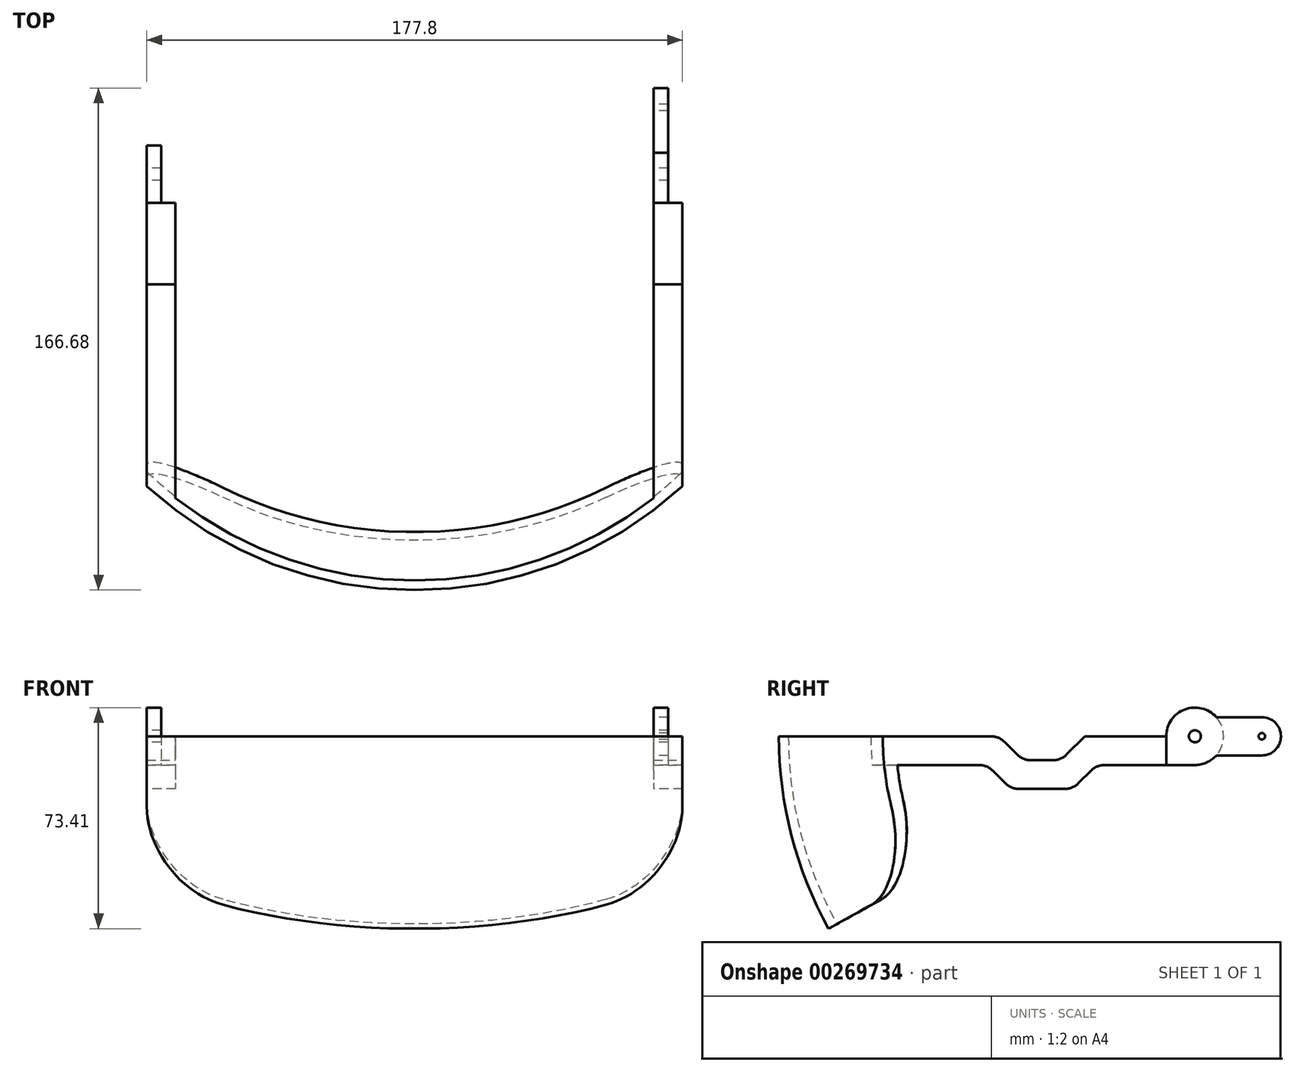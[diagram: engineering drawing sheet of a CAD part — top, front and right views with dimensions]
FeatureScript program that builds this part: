
annotation { "Feature Type Name" : "Feature", "Feature Type Description" : "" }
export const myFeature = defineFeature(function(context is Context, id is Id, definition is map)
    precondition{}
    {
        {
            var Q0;
            Q0=qCreatedBy(makeId("Right.planeOp"),FACE);
            var sketch = newSketch(context, id + "F0", { "sketchPlane" : qUnion([Q0])});
            skArc(sketch, "E0", {"start": v(0, 131.76) * mm, "mid": v(-131.76, 0) * mm, "end": v(0, -131.76) * mm});
            skArc(sketch, "E1", {"start": v(0, 128.59) * mm, "mid": v(-128.59, 0) * mm, "end": v(0, -128.59) * mm});
            skLineSegment(sketch, "E2", {"start": v(0, 131.76) * mm, "end": v(0, 0) * mm});
            skLineSegment(sketch, "E3.trimOffspring", {"start": v(0, -128.59) * mm, "end": v(0, -131.76) * mm});
            skPoint(sketch, "E4.orphan", {"position": v(0, 139.69) * mm});
            skSolve(sketch);
        }
        {
            var Q0;
            Q0=qSketchRegion(id+"F0",true);
            var Q1;
            Q1=sQuery(id+"F0.wireOp",EDGE,"E2");
            revolve(context, id + "F1", {"entities" : qUnion([Q0]), "axis" : qUnion([Q1]), "revolveType" : RevolveType.FULL});
        }
        {
            var Q0;
            Q0=qCreatedBy(makeId("Front.planeOp"),FACE);
            var sketch = newSketch(context, id + "F2", { "sketchPlane" : qUnion([Q0])});
            skLineSegment(sketch, "E5.left", {"start": v(88.9, 154.45) * mm, "end": v(88.9, -154.45) * mm});
            skLineSegment(sketch, "E5.right", {"start": v(-88.9, 154.45) * mm, "end": v(-88.9, -154.45) * mm});
            skPoint(sketch, "E5.middle", {"position": v(0, 0) * mm});
            skLineSegment(sketch, "E6.bottom", {"start": v(198.77, 154.45) * mm, "end": v(88.9, 154.45) * mm});
            skLineSegment(sketch, "E6.top", {"start": v(198.77, -154.45) * mm, "end": v(88.9, -154.45) * mm});
            skLineSegment(sketch, "E6.left", {"start": v(198.77, 154.45) * mm, "end": v(198.77, -154.45) * mm});
            skLineSegment(sketch, "E6.right", {"start": v(-198.77, 154.45) * mm, "end": v(-198.77, -154.45) * mm});
            skLineSegment(sketch, "E7.trimOffspring", {"start": v(-88.9, 154.45) * mm, "end": v(-198.77, 154.45) * mm});
            skPoint(sketch, "E5.bottom.end.orphan", {"position": v(-88.9, 227.43) * mm});
            skPoint(sketch, "E5.bottom.start.orphan", {"position": v(88.9, 227.43) * mm});
            skLineSegment(sketch, "E8.trimOffspring", {"start": v(-88.9, -154.45) * mm, "end": v(-198.77, -154.45) * mm});
            skPoint(sketch, "E5.top.start.orphan", {"position": v(88.9, -227.43) * mm});
            skPoint(sketch, "E9.orphan", {"position": v(-88.9, -227.43) * mm});
            skSolve(sketch);
        }
        {
            var Q0;
            Q0=qSketchRegion(id+"F2",true);
            extrude(context, id + "F3", {"entities" : qUnion([Q0]), "operationType" : NewBodyOperationType.REMOVE, "endBound" : BoundingType.SYMMETRIC, "depth" : 304.8 * mm});
        }
        {
            var Q0;
            Q0=qCreatedBy(makeId("Right.planeOp"),FACE);
            var sketch = newSketch(context, id + "F4", { "sketchPlane" : qUnion([Q0])});
            skLineSegment(sketch, "E10", {"start": v(0, 0) * mm, "end": v(-142.34, 0) * mm});
            skLineSegment(sketch, "E11", {"start": v(0, 0) * mm, "end": v(-124.79, -69.17) * mm});
            skArc(sketch, "E12", {"start": v(-124.79, -69.17) * mm, "mid": v(143.4, 35.68) * mm, "end": v(-142.34, 0) * mm});
            skSolve(sketch);
        }
        {
            var Q0;
            Q0=qSketchRegion(id+"F4",true);
            extrude(context, id + "F5", {"entities" : qUnion([Q0]), "operationType" : NewBodyOperationType.REMOVE, "endBound" : BoundingType.SYMMETRIC, "depth" : 304.8 * mm});
        }
        {
            var Q0;
            Q0=makeQuery(id+"F5.boolean.opBoolean","INTERSECT",EDGE,{"derivedFrom":[makeQuery(id+"F3.boolean.opBoolean","COPY",FACE,{"derivedFrom":makeQuery(id+"F3.opExtrude","SWEPT_FACE",FACE,{"disambiguationData":[OSD([sQuery(id+"F2.wireOp",EDGE,"E5.left")])]})}),makeQuery(id+"F5.opExtrude","SWEPT_FACE",FACE,{"disambiguationData":[OSD([sQuery(id+"F4.wireOp",EDGE,"E11")])]})]});
            var Q1;
            Q1=makeQuery(id+"F5.boolean.opBoolean","INTERSECT",EDGE,{"derivedFrom":[makeQuery(id+"F3.boolean.opBoolean","COPY",FACE,{"derivedFrom":makeQuery(id+"F3.opExtrude","SWEPT_FACE",FACE,{"disambiguationData":[OSD([sQuery(id+"F2.wireOp",EDGE,"E5.right")])]})}),makeQuery(id+"F5.opExtrude","SWEPT_FACE",FACE,{"disambiguationData":[OSD([sQuery(id+"F4.wireOp",EDGE,"E11")])]})]});
            fillet(context, id + "F6", {"entities" : qUnion([Q0, Q1]), "radius" : 25.4 * mm, "tangentPropagation" : true, "allowEdgeOverflow" : false});
        }
        {
            var Q0;
            Q0=qCreatedBy(makeId("Front.planeOp"),FACE);
            var sketch = newSketch(context, id + "F7", { "sketchPlane" : qUnion([Q0])});
            skLineSegment(sketch, "E13", {"start": v(88.9, 0) * mm, "end": v(88.9, -9.53) * mm});
            skLineSegment(sketch, "E14", {"start": v(88.9, -9.53) * mm, "end": v(79.38, -9.53) * mm});
            skLineSegment(sketch, "E15", {"start": v(79.38, -9.53) * mm, "end": v(79.38, 0) * mm});
            skLineSegment(sketch, "E16", {"start": v(79.38, 0) * mm, "end": v(88.9, 0) * mm});
            skLineSegment(sketch, "E17", {"start": v(-79.38, 0) * mm, "end": v(-79.38, -9.53) * mm});
            skLineSegment(sketch, "E18", {"start": v(-79.38, -9.53) * mm, "end": v(-88.9, -9.53) * mm});
            skLineSegment(sketch, "E19", {"start": v(-88.9, -9.53) * mm, "end": v(-88.9, 0) * mm});
            skLineSegment(sketch, "E20", {"start": v(-88.9, 0) * mm, "end": v(-79.38, 0) * mm});
            skSolve(sketch);
        }
        {
            var Q0;
            Q0=qSketchRegion(id+"F7",true);
            var Q1;
            Q1=makeQuery(id+"F1.opRevolve","SWEPT_FACE",FACE,{"disambiguationData":[OSD([sQuery(id+"F0.wireOp",EDGE,"E1")])]});
            extrude(context, id + "F8", {"entities" : qUnion([Q0]), "operationType" : NewBodyOperationType.ADD, "endBound" : BoundingType.UP_TO_SURFACE, "endBoundEntityFace" : qUnion([Q1]), "depth" : 25.4 * mm});
        }
        {
            var Q0;
            Q0=makeQuery(id+"F8.opExtrude","CAP_FACE",FACE,{"disambiguationData":[OSD([sQuery(id+"F7.wireOp",EDGE,"E13"),sQuery(id+"F7.wireOp",EDGE,"E14"),sQuery(id+"F7.wireOp",EDGE,"E15"),sQuery(id+"F7.wireOp",EDGE,"E16")])],"isStart":true});
            var sketch = newSketch(context, id + "F9", { "sketchPlane" : qUnion([Q0])});
            skLineSegment(sketch, "E21.bottom", {"start": v(-88.9, 0) * mm, "end": v(-79.38, 0) * mm});
            skLineSegment(sketch, "E21.top", {"start": v(-88.9, -9.53) * mm, "end": v(-79.38, -9.53) * mm});
            skLineSegment(sketch, "E21.left", {"start": v(-88.9, 0) * mm, "end": v(-88.9, -9.53) * mm});
            skLineSegment(sketch, "E21.right", {"start": v(-79.38, 0) * mm, "end": v(-79.38, -9.53) * mm});
            skSolve(sketch);
        }
        {
            var Q0;
            Q0=makeQuery(id+"F8.opExtrude","CAP_FACE",FACE,{"disambiguationData":[OSD([sQuery(id+"F7.wireOp",EDGE,"E17"),sQuery(id+"F7.wireOp",EDGE,"E18"),sQuery(id+"F7.wireOp",EDGE,"E19"),sQuery(id+"F7.wireOp",EDGE,"E20")])],"isStart":true});
            var sketch = newSketch(context, id + "F10", { "sketchPlane" : qUnion([Q0])});
            skLineSegment(sketch, "E22.bottom", {"start": v(79.38, 0) * mm, "end": v(88.9, 0) * mm});
            skLineSegment(sketch, "E22.top", {"start": v(79.38, -9.53) * mm, "end": v(88.9, -9.53) * mm});
            skLineSegment(sketch, "E22.left", {"start": v(79.38, 0) * mm, "end": v(79.38, -9.53) * mm});
            skLineSegment(sketch, "E22.right", {"start": v(88.9, 0) * mm, "end": v(88.9, -9.53) * mm});
            skSolve(sketch);
        }
        {
            var Q0;
            Q0 = qSketchRegion(id + "F9", true);
            var Q1;
            Q1 = qSketchRegion(id + "F10", true);
            extrude(context, id + "F11", {"entities" : qUnion([Q0, Q1]), "operationType" : NewBodyOperationType.ADD, "depth" : 6.35 * mm, "offsetDistance" : 25.4 * mm});
        }
        {
            var Q0;
            Q0=qCreatedBy(makeId("Right.planeOp"),FACE);
            var sketch = newSketch(context, id + "F12", { "sketchPlane" : qUnion([Q0])});
            skLineSegment(sketch, "E23", {"start": v(-16.7, 0) * mm, "end": v(-72.2, 0) * mm});
            skLineSegment(sketch, "E24", {"start": v(-34.93, -4.76) * mm, "end": v(-34.93, -9.52) * mm});
            skLineSegment(sketch, "E25", {"start": v(-53.98, -4.76) * mm, "end": v(-53.98, -7.94) * mm});
            skLineSegment(sketch, "E26", {"start": v(-58.57, -7.94) * mm, "end": v(-53.98, -7.94) * mm});
            skLineSegment(sketch, "E27", {"start": v(-34.93, -9.52) * mm, "end": v(-53.98, -9.52) * mm});
            skPoint(sketch, "E28.orphan", {"position": v(6.35, -4.76) * mm});
            skLineSegment(sketch, "E29", {"start": v(-53.98, -4.76) * mm, "end": v(-50.8, -7.94) * mm});
            skLineSegment(sketch, "E30", {"start": v(-34.93, -4.76) * mm, "end": v(-38.1, -7.94) * mm});
            skLineSegment(sketch, "E31", {"start": v(-72.2, 0) * mm, "end": v(-54.75, -17.46) * mm});
            skLineSegment(sketch, "E32", {"start": v(-16.7, 0) * mm, "end": v(-34.15, -17.46) * mm});
            skLineSegment(sketch, "E33", {"start": v(-54.75, -17.46) * mm, "end": v(-34.15, -17.46) * mm});
            skPoint(sketch, "E34.orphan", {"position": v(6.35, -9.52) * mm});
            skPoint(sketch, "E35.orphan", {"position": v(6.35, 0) * mm});
            skPoint(sketch, "E36.end.orphan", {"position": v(-30.16, 0) * mm});
            skLineSegment(sketch, "E37.trimOffspring", {"start": v(-50.8, -7.94) * mm, "end": v(-38.1, -7.94) * mm});
            skLineSegment(sketch, "E38.trimOffspring", {"start": v(-34.93, -7.94) * mm, "end": v(-30.24, -7.94) * mm});
            skSolve(sketch);
        }
        {
            var Q0;
            Q0=qSketchRegion(id+"F12",true);
            extrude(context, id + "F13", {"entities" : qUnion([Q0]), "operationType" : NewBodyOperationType.ADD, "endBound" : BoundingType.SYMMETRIC, "depth" : 177.8 * mm});
        }
        {
            var Q0;
            Q0=makeQuery(id+"F13.boolean.opBoolean","MERGE",FACE,{"derivedFrom":[makeQuery(id+"F8.boolean.opBoolean","MERGE",FACE,{"derivedFrom":[makeQuery(id+"F3.boolean.opBoolean","COPY",FACE,{"derivedFrom":makeQuery(id+"F3.opExtrude","SWEPT_FACE",FACE,{"disambiguationData":[OSD([sQuery(id+"F2.wireOp",EDGE,"E5.left")])]})}),makeQuery(id+"F8.opExtrude","SWEPT_FACE",FACE,{"disambiguationData":[OSD([sQuery(id+"F7.wireOp",EDGE,"E13")])]})]}),makeQuery(id+"F13.opExtrude","CAP_FACE",FACE,{"disambiguationData":[OSD([sQuery(id+"F12.wireOp",EDGE,"E23"),sQuery(id+"F12.wireOp",EDGE,"E31"),sQuery(id+"F12.wireOp",EDGE,"E32"),sQuery(id+"F12.wireOp",EDGE,"E33")])],"isStart":false})]});
            var sketch = newSketch(context, id + "F14", { "sketchPlane" : qUnion([Q0])});
            skLineSegment(sketch, "E39", {"start": v(-30.16, 0) * mm, "end": v(-58.74, 0) * mm});
            skLineSegment(sketch, "E40", {"start": v(-50.8, -7.94) * mm, "end": v(-38.1, -7.94) * mm});
            skLineSegment(sketch, "E41", {"start": v(-53.98, -4.76) * mm, "end": v(-58.74, 0) * mm});
            skLineSegment(sketch, "E42", {"start": v(-34.93, -4.76) * mm, "end": v(-30.16, 0) * mm});
            skLineSegment(sketch, "E43", {"start": v(-53.98, -4.76) * mm, "end": v(-50.8, -7.94) * mm});
            skLineSegment(sketch, "E44", {"start": v(-34.93, -4.76) * mm, "end": v(-38.1, -7.94) * mm});
            skPoint(sketch, "E45.orphan", {"position": v(6.35, -4.76) * mm});
            skSolve(sketch);
        }
        {
            var Q0;
            Q0=qSketchRegion(id+"F14",true);
            extrude(context, id + "F15", {"entities" : qUnion([Q0]), "operationType" : NewBodyOperationType.REMOVE, "oppositeDirection" : true, "depth" : 177.8 * mm});
        }
        {
            var Q0;
            Q0=qCreatedBy(makeId("Front.planeOp"),FACE);
            var sketch = newSketch(context, id + "F16", { "sketchPlane" : qUnion([Q0])});
            skLineSegment(sketch, "E46.bottom", {"start": v(-79.38, 25.4) * mm, "end": v(79.38, 25.4) * mm});
            skLineSegment(sketch, "E46.top", {"start": v(-79.38, -25.4) * mm, "end": v(79.38, -25.4) * mm});
            skLineSegment(sketch, "E46.left", {"start": v(-79.38, 25.4) * mm, "end": v(-79.38, -25.4) * mm});
            skLineSegment(sketch, "E46.right", {"start": v(79.38, 25.4) * mm, "end": v(79.38, -25.4) * mm});
            skPoint(sketch, "E46.middle", {"position": v(0, 0) * mm});
            skSolve(sketch);
        }
        {
            var Q0;
            Q0=qSketchRegion(id+"F16",true);
            extrude(context, id + "F17", {"entities" : qUnion([Q0]), "operationType" : NewBodyOperationType.REMOVE, "depth" : 82.55 * mm});
        }
        {
            var Q0;
            Q0=makeQuery(id+"F13.boolean.opBoolean","MERGE",FACE,{"derivedFrom":[makeQuery(id+"F8.boolean.opBoolean","MERGE",FACE,{"derivedFrom":[makeQuery(id+"F3.boolean.opBoolean","COPY",FACE,{"derivedFrom":makeQuery(id+"F3.opExtrude","SWEPT_FACE",FACE,{"disambiguationData":[OSD([sQuery(id+"F2.wireOp",EDGE,"E5.right")])]})}),makeQuery(id+"F8.opExtrude","SWEPT_FACE",FACE,{"disambiguationData":[OSD([sQuery(id+"F7.wireOp",EDGE,"E19")])]})]}),makeQuery(id+"F13.opExtrude","CAP_FACE",FACE,{"disambiguationData":[OSD([sQuery(id+"F12.wireOp",EDGE,"E23"),sQuery(id+"F12.wireOp",EDGE,"E31"),sQuery(id+"F12.wireOp",EDGE,"E32"),sQuery(id+"F12.wireOp",EDGE,"E33")])],"isStart":true})]});
            var sketch = newSketch(context, id + "F18", { "sketchPlane" : qUnion([Q0])});
            skCircle(sketch, "E47", {"center": v(-6.35, 0) * mm, "radius": 9.53 * mm});
            skSolve(sketch);
        }
        {
            var Q0;
            Q0=qSketchRegion(id+"F18",true);
            extrude(context, id + "F19", {"entities" : qUnion([Q0]), "operationType" : NewBodyOperationType.ADD, "oppositeDirection" : true, "depth" : 4.76 * mm});
        }
        {
            var Q0;
            {var subQ7=sQuery(id+"F7.wireOp",EDGE,"E15");var subQ8=makeQuery(id+"F8.opExtrude","SWEPT_FACE",FACE,{"disambiguationData":[OSD([subQ7])]});Q0=makeQuery(id+"F17.boolean.opBoolean","MERGE",FACE,{"derivedFrom":[makeQuery(id+"F13.boolean.opBoolean","SPLIT",FACE,{"disambiguationData":[TD([makeQuery(id+"F13.opExtrude","SWEPT_FACE",FACE,{"disambiguationData":[OSD([sQuery(id+"F12.wireOp",EDGE,"E32")])]})])],"derivedFrom":subQ8}),makeQuery(id+"F13.boolean.opBoolean","SPLIT",FACE,{"disambiguationData":[TD([makeQuery(id+"F1.opRevolve","SWEPT_FACE",FACE,{"disambiguationData":[OSD([sQuery(id+"F0.wireOp",EDGE,"E1")])]})])],"derivedFrom":subQ8}),makeQuery(id+"F17.opExtrude","SWEPT_FACE",FACE,{"disambiguationData":[OSD([sQuery(id+"F16.wireOp",EDGE,"E46.right")])]})]});}
            var sketch = newSketch(context, id + "F20", { "sketchPlane" : qUnion([Q0])});
            skCircle(sketch, "E48", {"center": v(-6.35, 0) * mm, "radius": 9.53 * mm});
            skSolve(sketch);
        }
        {
            var Q0;
            Q0=qSketchRegion(id+"F20",true);
            extrude(context, id + "F21", {"entities" : qUnion([Q0]), "operationType" : NewBodyOperationType.ADD, "oppositeDirection" : true, "depth" : 4.76 * mm});
        }
        {
            var Q0;
            Q0=makeQuery(id+"F21.opExtrude","CAP_FACE",FACE,{"disambiguationData":[OSD([sQuery(id+"F20.wireOp",EDGE,"E48")])],"isStart":false});
            var sketch = newSketch(context, id + "F22", { "sketchPlane" : qUnion([Q0])});
            skArc(sketch, "E49", {"start": v(6.35, -9.53) * mm, "mid": v(13.09, 6.74) * mm, "end": v(-3.18, 0) * mm});
            skLineSegment(sketch, "E50", {"start": v(-3.18, 0) * mm, "end": v(-3.18, -9.53) * mm});
            skLineSegment(sketch, "E51", {"start": v(-3.18, -9.53) * mm, "end": v(6.35, -9.53) * mm});
            skSolve(sketch);
        }
        {
            var Q0;
            Q0=qSketchRegion(id+"F22",true);
            extrude(context, id + "F23", {"entities" : qUnion([Q0]), "operationType" : NewBodyOperationType.REMOVE, "depth" : 4.76 * mm});
        }
        {
            var Q0;
            {var subQ7=sQuery(id+"F7.wireOp",EDGE,"E17");var subQ8=makeQuery(id+"F8.opExtrude","SWEPT_FACE",FACE,{"disambiguationData":[OSD([subQ7])]});Q0=makeQuery(id+"F17.boolean.opBoolean","MERGE",FACE,{"derivedFrom":[makeQuery(id+"F13.boolean.opBoolean","SPLIT",FACE,{"disambiguationData":[TD([makeQuery(id+"F13.opExtrude","SWEPT_FACE",FACE,{"disambiguationData":[OSD([sQuery(id+"F12.wireOp",EDGE,"E32")])]})])],"derivedFrom":subQ8}),makeQuery(id+"F13.boolean.opBoolean","SPLIT",FACE,{"disambiguationData":[TD([makeQuery(id+"F1.opRevolve","SWEPT_FACE",FACE,{"disambiguationData":[OSD([sQuery(id+"F0.wireOp",EDGE,"E1")])]})])],"derivedFrom":subQ8}),makeQuery(id+"F17.opExtrude","SWEPT_FACE",FACE,{"disambiguationData":[OSD([sQuery(id+"F16.wireOp",EDGE,"E46.left")])]})]});}
            var sketch = newSketch(context, id + "F24", { "sketchPlane" : qUnion([Q0])});
            skArc(sketch, "E52", {"start": v(6.35, -9.52) * mm, "mid": v(13.09, 6.74) * mm, "end": v(-3.17, 0) * mm});
            skLineSegment(sketch, "E53", {"start": v(-3.17, 0) * mm, "end": v(-3.17, -9.52) * mm});
            skLineSegment(sketch, "E54", {"start": v(-3.17, -9.52) * mm, "end": v(6.35, -9.52) * mm});
            skSolve(sketch);
        }
        {
            var Q0;
            Q0=qSketchRegion(id+"F24",true);
            extrude(context, id + "F25", {"entities" : qUnion([Q0]), "operationType" : NewBodyOperationType.REMOVE, "oppositeDirection" : true, "depth" : 4.76 * mm});
        }
        {
            var Q0;
            Q0=qCreatedBy(makeId("Right.planeOp"),FACE);
            var sketch = newSketch(context, id + "F26", { "sketchPlane" : qUnion([Q0])});
            skCircle(sketch, "E55", {"center": v(6.35, 0) * mm, "radius": 2 * mm});
            skSolve(sketch);
        }
        {
            var Q0;
            Q0=qSketchRegion(id+"F26",true);
            extrude(context, id + "F27", {"entities" : qUnion([Q0]), "operationType" : NewBodyOperationType.REMOVE, "endBound" : BoundingType.SYMMETRIC, "depth" : 177.8 * mm});
        }
        {
            var Q0;
            {var subQ0=sQuery(id+"F7.wireOp",EDGE,"E13");var subQ1=sQuery(id+"F4.wireOp",EDGE,"E10");var subQ2=sQuery(id+"F2.wireOp",EDGE,"E5.left");var subQ3=sQuery(id+"F7.wireOp",EDGE,"E16");var subQ4=sQuery(id+"F14.wireOp",EDGE,"E41");Q0=makeQuery(id+"F17.boolean.opBoolean","SPLIT",EDGE,{"disambiguationData":[TD([makeQuery(id+"F3.boolean.opBoolean","COPY",FACE,{"derivedFrom":makeQuery(id+"F3.opExtrude","SWEPT_FACE",FACE,{"disambiguationData":[OSD([subQ2])]})})])],"derivedFrom":makeQuery(id+"F15.boolean.opBoolean","COPY",EDGE,{"derivedFrom":makeQuery(id+"F15.opExtrude","SWEPT_EDGE",EDGE,{"disambiguationData":[OSD([subQ2,subQ1,subQ0,subQ3,sQuery(id+"F14.wireOp",EDGE,"E39"),subQ4])]})})});}
            var Q1;
            {var subQ0=sQuery(id+"F14.wireOp",EDGE,"E40");var subQ1=sQuery(id+"F14.wireOp",EDGE,"E43");Q1=makeQuery(id+"F17.boolean.opBoolean","SPLIT",EDGE,{"disambiguationData":[TD([makeQuery(id+"F3.boolean.opBoolean","COPY",FACE,{"derivedFrom":makeQuery(id+"F3.opExtrude","SWEPT_FACE",FACE,{"disambiguationData":[OSD([sQuery(id+"F2.wireOp",EDGE,"E5.left")])]})})])],"derivedFrom":makeQuery(id+"F15.boolean.opBoolean","COPY",EDGE,{"derivedFrom":makeQuery(id+"F15.opExtrude","SWEPT_EDGE",EDGE,{"disambiguationData":[OSD([subQ0,subQ1])]})})});}
            var Q2;
            {var subQ0=sQuery(id+"F14.wireOp",EDGE,"E40");var subQ1=sQuery(id+"F14.wireOp",EDGE,"E44");Q2=makeQuery(id+"F17.boolean.opBoolean","SPLIT",EDGE,{"disambiguationData":[TD([makeQuery(id+"F3.boolean.opBoolean","COPY",FACE,{"derivedFrom":makeQuery(id+"F3.opExtrude","SWEPT_FACE",FACE,{"disambiguationData":[OSD([sQuery(id+"F2.wireOp",EDGE,"E5.left")])]})})])],"derivedFrom":makeQuery(id+"F15.boolean.opBoolean","COPY",EDGE,{"derivedFrom":makeQuery(id+"F15.opExtrude","SWEPT_EDGE",EDGE,{"disambiguationData":[OSD([subQ0,subQ1])]})})});}
            var Q3;
            {var subQ0=sQuery(id+"F7.wireOp",EDGE,"E13");var subQ1=sQuery(id+"F4.wireOp",EDGE,"E10");var subQ2=sQuery(id+"F2.wireOp",EDGE,"E5.left");var subQ3=sQuery(id+"F7.wireOp",EDGE,"E16");var subQ5=sQuery(id+"F14.wireOp",EDGE,"E42");Q3=makeQuery(id+"F17.boolean.opBoolean","SPLIT",EDGE,{"disambiguationData":[TD([makeQuery(id+"F3.boolean.opBoolean","COPY",FACE,{"derivedFrom":makeQuery(id+"F3.opExtrude","SWEPT_FACE",FACE,{"disambiguationData":[OSD([subQ2])]})})])],"derivedFrom":makeQuery(id+"F15.boolean.opBoolean","COPY",EDGE,{"derivedFrom":makeQuery(id+"F15.opExtrude","SWEPT_EDGE",EDGE,{"disambiguationData":[OSD([subQ2,subQ1,subQ0,subQ3,sQuery(id+"F14.wireOp",EDGE,"E39"),subQ5])]})})});}
            var Q4;
            Q4=makeQuery(id+"F23.boolean.opBoolean","COPY",EDGE,{"derivedFrom":makeQuery(id+"F23.opExtrude","CAP_EDGE",EDGE,{"disambiguationData":[OSD([sQuery(id+"F22.wireOp",EDGE,"E50")])],"isStart":false})});
            var Q5;
            Q5=makeQuery(id+"F13.boolean.opBoolean","INTERSECT",EDGE,{"derivedFrom":[makeQuery(id+"F8.opExtrude","SWEPT_FACE",FACE,{"disambiguationData":[OSD([sQuery(id+"F7.wireOp",EDGE,"E14")])]}),makeQuery(id+"F13.opExtrude","SWEPT_FACE",FACE,{"disambiguationData":[OSD([sQuery(id+"F12.wireOp",EDGE,"E32")])]})]});
            var Q6;
            {var subQ0=sQuery(id+"F12.wireOp",EDGE,"E33");var subQ1=sQuery(id+"F12.wireOp",EDGE,"E32");Q6=makeQuery(id+"F17.boolean.opBoolean","SPLIT",EDGE,{"disambiguationData":[TD([makeQuery(id+"F3.boolean.opBoolean","COPY",FACE,{"derivedFrom":makeQuery(id+"F3.opExtrude","SWEPT_FACE",FACE,{"disambiguationData":[OSD([sQuery(id+"F2.wireOp",EDGE,"E5.left")])]})})])],"derivedFrom":makeQuery(id+"F13.opExtrude","SWEPT_EDGE",EDGE,{"disambiguationData":[OSD([subQ1,subQ0])]})});}
            var Q7;
            {var subQ0=sQuery(id+"F12.wireOp",EDGE,"E33");var subQ1=sQuery(id+"F12.wireOp",EDGE,"E31");Q7=makeQuery(id+"F17.boolean.opBoolean","SPLIT",EDGE,{"disambiguationData":[TD([makeQuery(id+"F3.boolean.opBoolean","COPY",FACE,{"derivedFrom":makeQuery(id+"F3.opExtrude","SWEPT_FACE",FACE,{"disambiguationData":[OSD([sQuery(id+"F2.wireOp",EDGE,"E5.left")])]})})])],"derivedFrom":makeQuery(id+"F13.opExtrude","SWEPT_EDGE",EDGE,{"disambiguationData":[OSD([subQ1,subQ0])]})});}
            var Q8;
            Q8=makeQuery(id+"F13.boolean.opBoolean","INTERSECT",EDGE,{"derivedFrom":[makeQuery(id+"F8.opExtrude","SWEPT_FACE",FACE,{"disambiguationData":[OSD([sQuery(id+"F7.wireOp",EDGE,"E14")])]}),makeQuery(id+"F13.opExtrude","SWEPT_FACE",FACE,{"disambiguationData":[OSD([sQuery(id+"F12.wireOp",EDGE,"E31")])]})]});
            var Q9;
            Q9=makeQuery(id+"F8.opExtrude","TWEAK_EDGE",EDGE,{"derivedFrom":[makeQuery(id+"F1.opRevolve","SWEPT_FACE",FACE,{"disambiguationData":[OSD([sQuery(id+"F0.wireOp",EDGE,"E1")])]}),makeQuery(id+"F7.imprint","IMPRINT",EDGE,{"derivedFrom":sQuery(id+"F7.wireOp",EDGE,"E14")})]});
            var Q10;
            {var subQ0=sQuery(id+"F7.wireOp",EDGE,"E16");var subQ1=sQuery(id+"F14.wireOp",EDGE,"E41");var subQ3=sQuery(id+"F4.wireOp",EDGE,"E10");Q10=makeQuery(id+"F17.boolean.opBoolean","SPLIT",EDGE,{"disambiguationData":[TD([makeQuery(id+"F3.boolean.opBoolean","COPY",FACE,{"derivedFrom":makeQuery(id+"F3.opExtrude","SWEPT_FACE",FACE,{"disambiguationData":[OSD([sQuery(id+"F2.wireOp",EDGE,"E5.right")])]})})])],"derivedFrom":makeQuery(id+"F15.boolean.opBoolean","COPY",EDGE,{"derivedFrom":makeQuery(id+"F15.opExtrude","SWEPT_EDGE",EDGE,{"disambiguationData":[OSD([sQuery(id+"F2.wireOp",EDGE,"E5.left"),subQ3,sQuery(id+"F7.wireOp",EDGE,"E13"),subQ0,sQuery(id+"F14.wireOp",EDGE,"E39"),subQ1])]})})});}
            var Q11;
            {var subQ0=sQuery(id+"F14.wireOp",EDGE,"E40");var subQ1=sQuery(id+"F14.wireOp",EDGE,"E43");Q11=makeQuery(id+"F17.boolean.opBoolean","SPLIT",EDGE,{"disambiguationData":[TD([makeQuery(id+"F3.boolean.opBoolean","COPY",FACE,{"derivedFrom":makeQuery(id+"F3.opExtrude","SWEPT_FACE",FACE,{"disambiguationData":[OSD([sQuery(id+"F2.wireOp",EDGE,"E5.right")])]})})])],"derivedFrom":makeQuery(id+"F15.boolean.opBoolean","COPY",EDGE,{"derivedFrom":makeQuery(id+"F15.opExtrude","SWEPT_EDGE",EDGE,{"disambiguationData":[OSD([subQ0,subQ1])]})})});}
            var Q12;
            {var subQ0=sQuery(id+"F14.wireOp",EDGE,"E44");var subQ1=sQuery(id+"F14.wireOp",EDGE,"E40");Q12=makeQuery(id+"F17.boolean.opBoolean","SPLIT",EDGE,{"disambiguationData":[TD([makeQuery(id+"F3.boolean.opBoolean","COPY",FACE,{"derivedFrom":makeQuery(id+"F3.opExtrude","SWEPT_FACE",FACE,{"disambiguationData":[OSD([sQuery(id+"F2.wireOp",EDGE,"E5.right")])]})})])],"derivedFrom":makeQuery(id+"F15.boolean.opBoolean","COPY",EDGE,{"derivedFrom":makeQuery(id+"F15.opExtrude","SWEPT_EDGE",EDGE,{"disambiguationData":[OSD([subQ1,subQ0])]})})});}
            var Q13;
            {var subQ0=sQuery(id+"F7.wireOp",EDGE,"E16");var subQ2=sQuery(id+"F14.wireOp",EDGE,"E42");var subQ3=sQuery(id+"F4.wireOp",EDGE,"E10");Q13=makeQuery(id+"F17.boolean.opBoolean","SPLIT",EDGE,{"disambiguationData":[TD([makeQuery(id+"F3.boolean.opBoolean","COPY",FACE,{"derivedFrom":makeQuery(id+"F3.opExtrude","SWEPT_FACE",FACE,{"disambiguationData":[OSD([sQuery(id+"F2.wireOp",EDGE,"E5.right")])]})})])],"derivedFrom":makeQuery(id+"F15.boolean.opBoolean","COPY",EDGE,{"derivedFrom":makeQuery(id+"F15.opExtrude","SWEPT_EDGE",EDGE,{"disambiguationData":[OSD([sQuery(id+"F2.wireOp",EDGE,"E5.left"),subQ3,sQuery(id+"F7.wireOp",EDGE,"E13"),subQ0,sQuery(id+"F14.wireOp",EDGE,"E39"),subQ2])]})})});}
            var Q14;
            Q14=makeQuery(id+"F13.boolean.opBoolean","INTERSECT",EDGE,{"derivedFrom":[makeQuery(id+"F8.opExtrude","SWEPT_FACE",FACE,{"disambiguationData":[OSD([sQuery(id+"F7.wireOp",EDGE,"E18")])]}),makeQuery(id+"F13.opExtrude","SWEPT_FACE",FACE,{"disambiguationData":[OSD([sQuery(id+"F12.wireOp",EDGE,"E32")])]})]});
            var Q15;
            {var subQ0=sQuery(id+"F12.wireOp",EDGE,"E33");var subQ1=sQuery(id+"F12.wireOp",EDGE,"E32");Q15=makeQuery(id+"F17.boolean.opBoolean","SPLIT",EDGE,{"disambiguationData":[TD([makeQuery(id+"F3.boolean.opBoolean","COPY",FACE,{"derivedFrom":makeQuery(id+"F3.opExtrude","SWEPT_FACE",FACE,{"disambiguationData":[OSD([sQuery(id+"F2.wireOp",EDGE,"E5.right")])]})})])],"derivedFrom":makeQuery(id+"F13.opExtrude","SWEPT_EDGE",EDGE,{"disambiguationData":[OSD([subQ1,subQ0])]})});}
            var Q16;
            {var subQ0=sQuery(id+"F12.wireOp",EDGE,"E31");var subQ1=sQuery(id+"F12.wireOp",EDGE,"E33");Q16=makeQuery(id+"F17.boolean.opBoolean","SPLIT",EDGE,{"disambiguationData":[TD([makeQuery(id+"F3.boolean.opBoolean","COPY",FACE,{"derivedFrom":makeQuery(id+"F3.opExtrude","SWEPT_FACE",FACE,{"disambiguationData":[OSD([sQuery(id+"F2.wireOp",EDGE,"E5.right")])]})})])],"derivedFrom":makeQuery(id+"F13.opExtrude","SWEPT_EDGE",EDGE,{"disambiguationData":[OSD([subQ0,subQ1])]})});}
            var Q17;
            Q17=makeQuery(id+"F13.boolean.opBoolean","INTERSECT",EDGE,{"derivedFrom":[makeQuery(id+"F8.opExtrude","SWEPT_FACE",FACE,{"disambiguationData":[OSD([sQuery(id+"F7.wireOp",EDGE,"E18")])]}),makeQuery(id+"F13.opExtrude","SWEPT_FACE",FACE,{"disambiguationData":[OSD([sQuery(id+"F12.wireOp",EDGE,"E31")])]})]});
            var Q18;
            Q18=makeQuery(id+"F8.opExtrude","TWEAK_EDGE",EDGE,{"derivedFrom":[makeQuery(id+"F1.opRevolve","SWEPT_FACE",FACE,{"disambiguationData":[OSD([sQuery(id+"F0.wireOp",EDGE,"E1")])]}),makeQuery(id+"F7.imprint","IMPRINT",EDGE,{"derivedFrom":sQuery(id+"F7.wireOp",EDGE,"E18")})]});
            var Q19;
            Q19=makeQuery(id+"F25.boolean.opBoolean","COPY",EDGE,{"derivedFrom":makeQuery(id+"F25.opExtrude","CAP_EDGE",EDGE,{"disambiguationData":[OSD([sQuery(id+"F24.wireOp",EDGE,"E53")])],"isStart":true})});
            fillet(context, id + "F28", {"entities" : qUnion([Q0, Q1, Q2, Q3, Q4, Q5, Q6, Q7, Q8, Q9, Q10, Q11, Q12, Q13, Q14, Q15, Q16, Q17, Q18, Q19]), "radius" : 6.35 * mm, "tangentPropagation" : true, "allowEdgeOverflow" : false});
        }
        {
            var Q0;
            {var subQ7=sQuery(id+"F7.wireOp",EDGE,"E15");var subQ8=makeQuery(id+"F8.opExtrude","SWEPT_FACE",FACE,{"disambiguationData":[OSD([subQ7])]});Q0=makeQuery(id+"F21.boolean.opBoolean","MERGE",FACE,{"derivedFrom":[makeQuery(id+"F17.boolean.opBoolean","MERGE",FACE,{"derivedFrom":[makeQuery(id+"F13.boolean.opBoolean","SPLIT",FACE,{"disambiguationData":[TD([makeQuery(id+"F13.opExtrude","SWEPT_FACE",FACE,{"disambiguationData":[OSD([sQuery(id+"F12.wireOp",EDGE,"E32")])]})])],"derivedFrom":subQ8}),makeQuery(id+"F13.boolean.opBoolean","SPLIT",FACE,{"disambiguationData":[TD([makeQuery(id+"F1.opRevolve","SWEPT_FACE",FACE,{"disambiguationData":[OSD([sQuery(id+"F0.wireOp",EDGE,"E1")])]})])],"derivedFrom":subQ8}),makeQuery(id+"F17.opExtrude","SWEPT_FACE",FACE,{"disambiguationData":[OSD([sQuery(id+"F16.wireOp",EDGE,"E46.right")])]})]}),makeQuery(id+"F21.opExtrude","CAP_FACE",FACE,{"disambiguationData":[OSD([sQuery(id+"F20.wireOp",EDGE,"E48")])],"isStart":true})]});}
            var sketch = newSketch(context, id + "F29", { "sketchPlane" : qUnion([Q0])});
            skLineSegment(sketch, "E56.bottom", {"start": v(-28.58, -6.35) * mm, "end": v(-6.35, -6.35) * mm});
            skLineSegment(sketch, "E56.top", {"start": v(-28.57, 6.35) * mm, "end": v(-6.35, 6.35) * mm});
            skPoint(sketch, "E56.middle", {"position": v(-6.35, 0) * mm});
            skArc(sketch, "E57", {"start": v(-6.35, 2) * mm, "mid": v(-8.35, 0) * mm, "end": v(-6.35, -2) * mm});
            skLineSegment(sketch, "E58", {"start": v(-6.35, 6.35) * mm, "end": v(-6.35, 2) * mm});
            skPoint(sketch, "E59", {"position": v(-28.57, 6.35) * mm});
            skArc(sketch, "E60", {"start": v(-28.57, 6.35) * mm, "mid": v(-34.92, 0) * mm, "end": v(-28.58, -6.35) * mm});
            skPoint(sketch, "E61.orphan", {"position": v(-34.92, 6.35) * mm});
            skPoint(sketch, "E62.orphan", {"position": v(-34.93, -6.35) * mm});
            skPoint(sketch, "E56.right.end.orphan", {"position": v(22.23, 6.35) * mm});
            skPoint(sketch, "E63.orphan", {"position": v(22.22, -6.35) * mm});
            skLineSegment(sketch, "E64.trimOffspring", {"start": v(-6.35, -2) * mm, "end": v(-6.35, -6.35) * mm});
            skCircle(sketch, "E65", {"center": v(-28.58, 0) * mm, "radius": 1.08 * mm});
            skSolve(sketch);
        }
        {
            var Q0;
            Q0=qSketchRegion(id+"F29",true);
            extrude(context, id + "F30", {"entities" : qUnion([Q0]), "operationType" : NewBodyOperationType.ADD, "oppositeDirection" : true, "depth" : 4.76 * mm});
        }
    });
